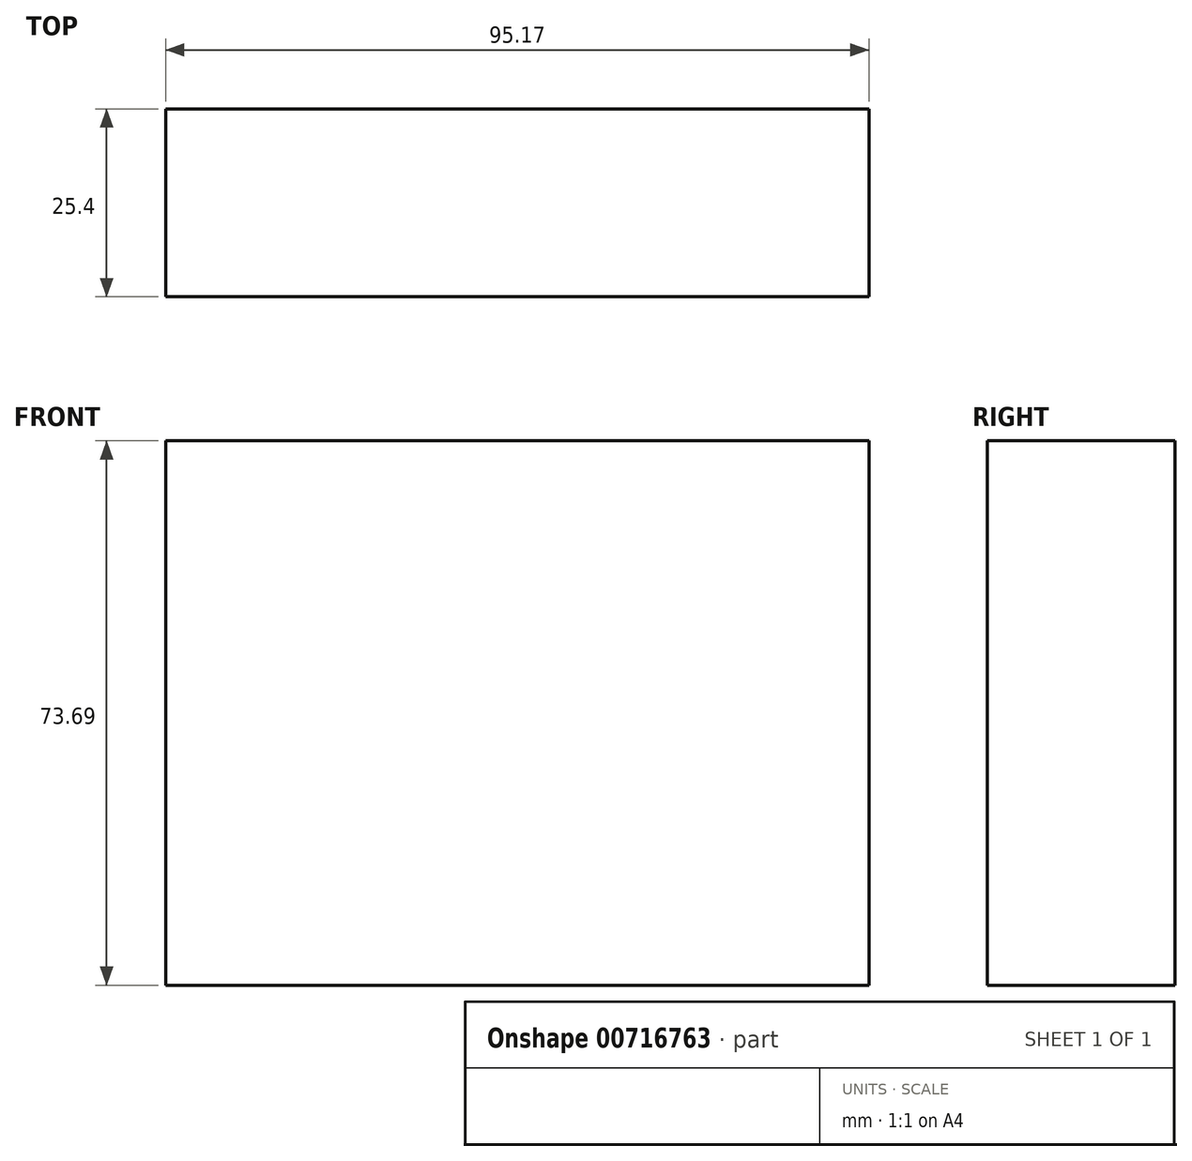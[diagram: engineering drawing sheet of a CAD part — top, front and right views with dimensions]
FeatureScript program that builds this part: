
annotation { "Feature Type Name" : "Feature", "Feature Type Description" : "" }
export const myFeature = defineFeature(function(context is Context, id is Id, definition is map)
    precondition{}
    {
        {
            var Q0;
            Q0=qCreatedBy(makeId("Front.planeOp"),FACE);
            var sketch = newSketch(context, id + "F0", { "sketchPlane" : qUnion([Q0])});
            skLineSegment(sketch, "E0.bottom", {"start": v(-57.63, 47.34) * mm, "end": v(37.54, 47.34) * mm});
            skLineSegment(sketch, "E0.top", {"start": v(-57.63, -26.35) * mm, "end": v(37.54, -26.35) * mm});
            skLineSegment(sketch, "E0.left", {"start": v(-57.63, 47.34) * mm, "end": v(-57.63, -26.35) * mm});
            skLineSegment(sketch, "E0.right", {"start": v(37.54, 47.34) * mm, "end": v(37.54, -26.35) * mm});
            skSolve(sketch);
        }
        {
            var Q0;
            Q0 = qSketchRegion(id + "F0", true);
            extrude(context, id + "F1", {"entities" : qUnion([Q0]), "depth" : 25.4 * mm, "offsetDistance" : 25.4 * mm});
        }
    });
